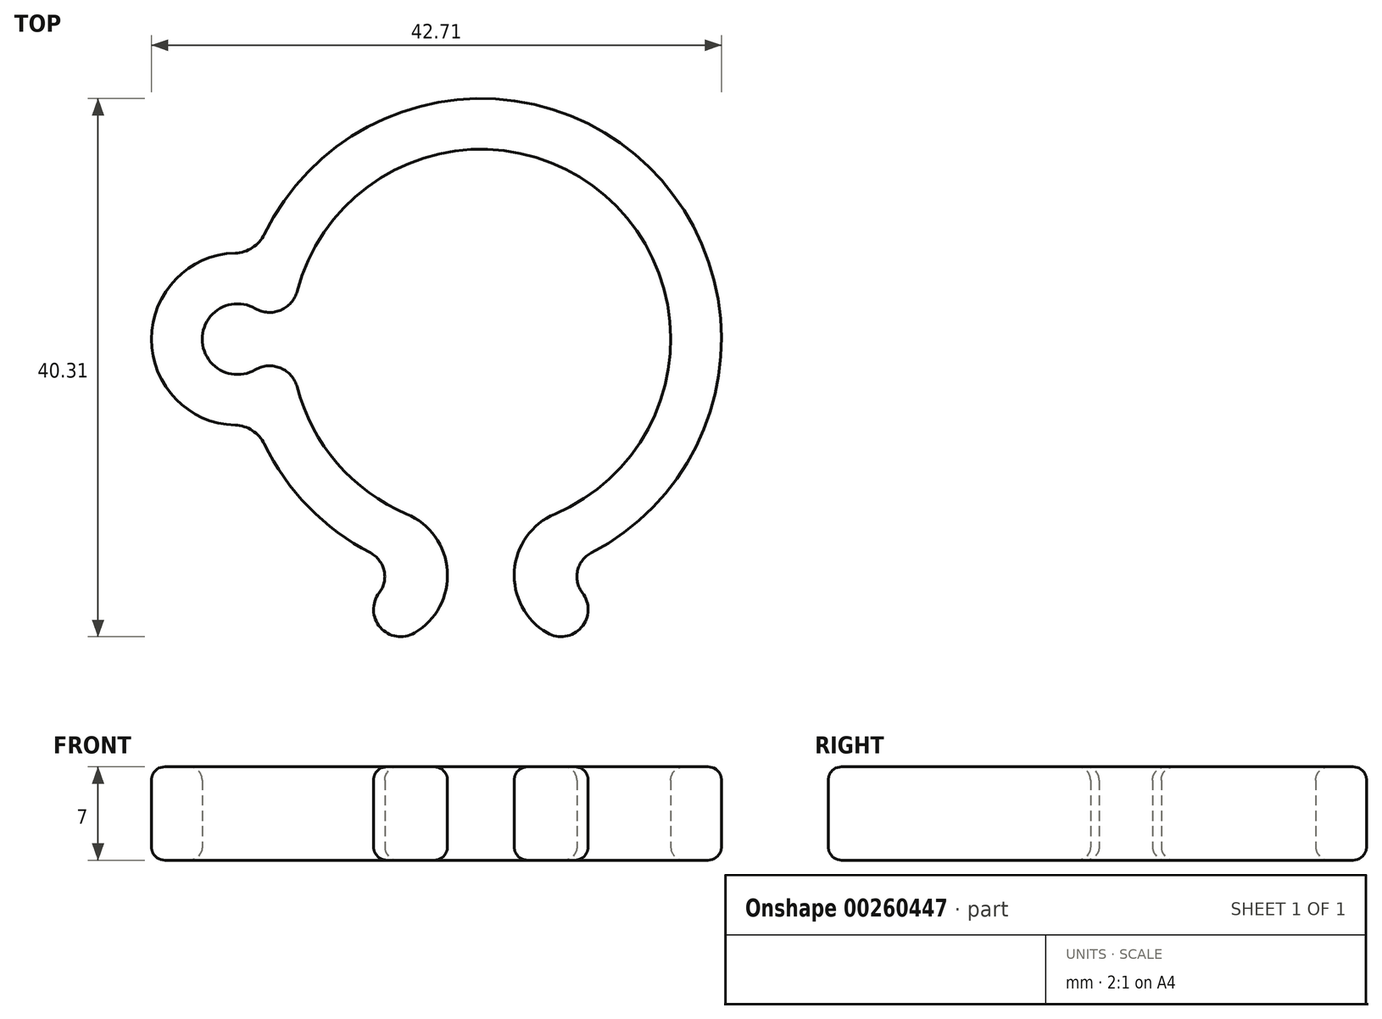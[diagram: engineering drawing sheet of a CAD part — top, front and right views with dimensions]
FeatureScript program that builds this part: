
annotation { "Feature Type Name" : "Feature", "Feature Type Description" : "" }
export const myFeature = defineFeature(function(context is Context, id is Id, definition is map)
    precondition{}
    {
        {
            var Q0;
            Q0=qCreatedBy(makeId("Top.planeOp"),FACE);
            var sketch = newSketch(context, id + "F0", { "sketchPlane" : qUnion([Q0])});
            skArc(sketch, "E0", {"start": v(-13.77, -3.59) * mm, "mid": v(14.23, 0) * mm, "end": v(-13.77, 3.59) * mm});
            skArc(sketch, "E1", {"start": v(-16.22, -7.86) * mm, "mid": v(-12.91, -12.58) * mm, "end": v(-8.28, -16.01) * mm});
            skArc(sketch, "E2", {"start": v(-4.97, -22.01) * mm, "mid": v(-2.51, -17.38) * mm, "end": v(-5.55, -13.1) * mm});
            skArc(sketch, "E3", {"start": v(-7.61, -19.01) * mm, "mid": v(-7.24, -17.36) * mm, "end": v(-8.28, -16.01) * mm});
            skArc(sketch, "E4", {"start": v(-7.61, -19.01) * mm, "mid": v(-7.53, -21.6) * mm, "end": v(-4.97, -22.01) * mm});
            skArc(sketch, "E5", {"start": v(-16.9, 2.29) * mm, "mid": v(-15, 2.16) * mm, "end": v(-13.77, 3.59) * mm});
            skLineSegment(sketch, "E6", {"start": v(0, 0) * mm, "end": v(0, -14.22) * mm, "construction": true});
            skLineSegment(sketch, "E7", {"start": v(0, 0) * mm, "end": v(-14.23, 0) * mm, "construction": true});
            skArc(sketch, "E8", {"start": v(-16.9, 2.29) * mm, "mid": v(-20.87, 0) * mm, "end": v(-16.9, -2.29) * mm});
            skPoint(sketch, "E9", {"position": v(-7.11, 0) * mm});
            skArc(sketch, "E10", {"start": v(-18.4, 6.45) * mm, "mid": v(-17.12, 6.85) * mm, "end": v(-16.22, 7.86) * mm});
            skArc(sketch, "E11.MirrorCS", {"start": v(-18.4, -6.45) * mm, "mid": v(-17.12, -6.85) * mm, "end": v(-16.22, -7.86) * mm});
            skArc(sketch, "E12", {"start": v(-18.4, 6.45) * mm, "mid": v(-24.67, 0) * mm, "end": v(-18.4, -6.45) * mm});
            skLineSegment(sketch, "E13", {"start": v(14.22, 0) * mm, "end": v(18.02, 0) * mm, "construction": true});
            skLineSegment(sketch, "E14", {"start": v(-20.87, 0) * mm, "end": v(-24.67, 0) * mm, "construction": true});
            skArc(sketch, "E15.MirrorCS", {"start": v(-16.9, -2.29) * mm, "mid": v(-15, -2.16) * mm, "end": v(-13.77, -3.59) * mm});
            skArc(sketch, "E16.MirrorCS", {"start": v(7.61, -19.01) * mm, "mid": v(7.53, -21.6) * mm, "end": v(4.97, -22.01) * mm});
            skArc(sketch, "E17.MirrorCS", {"start": v(7.61, -19.01) * mm, "mid": v(7.24, -17.36) * mm, "end": v(8.28, -16.01) * mm});
            skArc(sketch, "E18.MirrorCS", {"start": v(4.97, -22.01) * mm, "mid": v(2.51, -17.38) * mm, "end": v(5.55, -13.1) * mm});
            skArc(sketch, "E19.trimOffspring", {"start": v(8.28, -16.01) * mm, "mid": v(12.58, 12.91) * mm, "end": v(-16.22, 7.86) * mm});
            skSolve(sketch);
        }
        {
            var Q0;
            Q0=makeQuery(id+"F0.imprint","IMPRINT",FACE,{"disambiguationData":[TD([[makeQuery(id+"F0.imprint","IMPRINT",EDGE,{"derivedFrom":sQuery(id+"F0.wireOp",EDGE,"E1")}),1.0]])]});
            extrude(context, id + "F1", {"entities" : qUnion([Q0]), "depth" : 7 * mm, "offsetDistance" : 25 * mm});
        }
        {
            var Q0;
            Q0=makeQuery(id+"F1.opExtrude","CAP_FACE",FACE,{"disambiguationData":[OSD([sQuery(id+"F0.wireOp",EDGE,"E0"),sQuery(id+"F0.wireOp",EDGE,"E1"),sQuery(id+"F0.wireOp",EDGE,"E2"),sQuery(id+"F0.wireOp",EDGE,"E3"),sQuery(id+"F0.wireOp",EDGE,"E4"),sQuery(id+"F0.wireOp",EDGE,"E5"),sQuery(id+"F0.wireOp",EDGE,"E8"),sQuery(id+"F0.wireOp",EDGE,"E10"),sQuery(id+"F0.wireOp",EDGE,"E11.MirrorCS"),sQuery(id+"F0.wireOp",EDGE,"E12"),sQuery(id+"F0.wireOp",EDGE,"E15.MirrorCS"),sQuery(id+"F0.wireOp",EDGE,"E16.MirrorCS"),sQuery(id+"F0.wireOp",EDGE,"E17.MirrorCS"),sQuery(id+"F0.wireOp",EDGE,"E18.MirrorCS"),sQuery(id+"F0.wireOp",EDGE,"E19.trimOffspring")])],"isStart":false});
            var Q1;
            Q1=makeQuery(id+"F1.opExtrude","CAP_FACE",FACE,{"disambiguationData":[OSD([sQuery(id+"F0.wireOp",EDGE,"E0"),sQuery(id+"F0.wireOp",EDGE,"E1"),sQuery(id+"F0.wireOp",EDGE,"E2"),sQuery(id+"F0.wireOp",EDGE,"E3"),sQuery(id+"F0.wireOp",EDGE,"E4"),sQuery(id+"F0.wireOp",EDGE,"E5"),sQuery(id+"F0.wireOp",EDGE,"E8"),sQuery(id+"F0.wireOp",EDGE,"E10"),sQuery(id+"F0.wireOp",EDGE,"E11.MirrorCS"),sQuery(id+"F0.wireOp",EDGE,"E12"),sQuery(id+"F0.wireOp",EDGE,"E15.MirrorCS"),sQuery(id+"F0.wireOp",EDGE,"E16.MirrorCS"),sQuery(id+"F0.wireOp",EDGE,"E17.MirrorCS"),sQuery(id+"F0.wireOp",EDGE,"E18.MirrorCS"),sQuery(id+"F0.wireOp",EDGE,"E19.trimOffspring")])],"isStart":true});
            fillet(context, id + "F2", {"entities" : qUnion([Q0, Q1]), "radius" : 1 * mm, "tangentPropagation" : true, "allowEdgeOverflow" : false});
        }
    });
